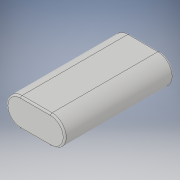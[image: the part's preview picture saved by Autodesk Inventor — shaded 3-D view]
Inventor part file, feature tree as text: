
AUTODESK INVENTOR PART (.ipt)
format: ipt  version: 2019 (Build 230136000, 136)  size: 121,344 bytes
history: native  units: mm
features: fillet x2, extrude x1, sketch x1
ambient origin geometry x8: Origin, YZ Plane, XZ Plane, XY Plane, X Axis, Y Axis, Z Axis, Center Point
bodies: Solid1 (feature_tree)
feature tree (4):
  extrude  "Extrusion1"  Depth=69.0mm
  fillet  "Fillet1"  Radius=18.0mm
  fillet  "Fillet2"  Radius=9.0mm
  sketch  "Sketch1"  dims[d0=37.0mm d1=69.0mm d2=18.0mm d3=0.0mm d4=9.0mm d5=1.0mm]
